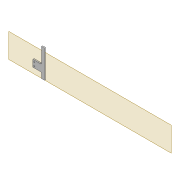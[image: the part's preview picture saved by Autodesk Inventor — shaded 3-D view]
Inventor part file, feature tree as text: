
AUTODESK INVENTOR PART (.ipt)
format: ipt  version: 2022 (Build 260153000, 153)  size: 493,568 bytes
history: native  units: mm
features: sketch x9, projected_geometry x9, extrude x8, fillet x2, shell x1, plane x1, chamfer x1
ambient origin geometry x8: Origin, YZ Plane, XZ Plane, XY Plane, X Axis, Y Axis, Z Axis, Center Point
bodies: Solid1 (feature_tree)
feature tree (31):
  extrude  "Extrusion1"  Depth=2.0mm
  shell  "Shell1"  Thickness=2.0mm
  extrude  "Extrusion8"  Depth=2.0mm
  extrude  "Extrusion3"  Depth=10.0mm TaperAngle=0.0deg
  extrude  "Extrusion4"  Depth=2.0mm
  fillet  "Fillet1"  Radius=5.0mm
  sketch  "Sketch10"  dims[d22=2.0mm d23=0.0mm d31=2.0mm d32=5.0mm]
  extrude  "Extrusion5"  Depth=2.5mm
  plane  "Work Plane2"
  extrude  "Extrusion9"  Depth=5.0mm
  fillet  "Fillet2"  Radius=2.5mm
  extrude  "Extrusion10"  Depth=5.0mm
  chamfer  "Chamfer1"  Distance=2.0mm
  extrude  "Extrusion12"  Depth=12.0mm
  sketch  "Sketch30"  dims[d66=2.5mm d67=12.0mm]
  sketch  "Sketch31"  dims[d68=5.0mm d69=15.0mm d70=12.0mm d71=3.05mm d72=10.0mm d73=0.0mm d74=2.0mm d75=90.0mm d76=20.0mm d77=0.5mm d78=10.0mm d79=0.0mm d82=10.0mm d83=3.0mm d84=2.0mm d85=45.0deg d86=0.0mm d87=1.0mm d88=1.0mm d89=1.0mm d90=1.0mm d91=1.0mm d92=10.0mm d93=0.0mm]
  sketch  "Sketch3"  dims[d0=2.0mm d1=0.0mm d2=4.0mm d7=2.0mm]
  sketch  "Sketch8"  dims[d8=2.0mm d9=5.9mm]
  sketch  "Sketch9"  dims[d13=10.0mm d14=0.0mm d16=10.0mm d17=0.0mm]
  projected_geometry  "Projected Loop4"
  projected_geometry  "Projected Loop10"
  sketch  "Sketch24"  dims[d34=1.6mm d35=2.5mm]
  projected_geometry  "Projected Loop11"
  projected_geometry  "Projected Loop12"
  projected_geometry  "Projected Loop13"
  sketch  "Sketch26"  dims[d37=5.0mm d38=1.6mm d40=2.5mm]
  projected_geometry  "Projected Loop14"
  sketch  "Sketch29"  dims[d62=80.0mm d63=5.0mm d64=2.0mm d65=0.0mm]
  projected_geometry  "Project Cut Edges1"
  projected_geometry  "Project Cut Edges2"
  projected_geometry  "Project Cut Edges3"
